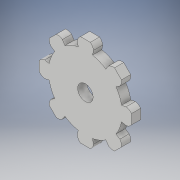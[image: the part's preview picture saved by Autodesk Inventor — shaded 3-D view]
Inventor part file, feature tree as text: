
AUTODESK INVENTOR PART (.ipt)
format: ipt  version: 2017 (Build 210142000, 142)  size: 165,376 bytes
history: native  units: in
note: dims shown in document units (in); Inventor stores cm internally (conversion verified against a paired STEP export)
features: extrude x2, sketch x2, pattern_circular x1
ambient origin geometry x8: Origin, YZ Plane, XZ Plane, XY Plane, X Axis, Y Axis, Z Axis, Center Point
bodies: Solid1 (feature_tree)
feature tree (5):
  extrude  "Extrusion1"  Depth=0.075in TaperAngle=0.0deg
  pattern_circular  "Circular Pattern1"  Count=8 Angle=360.0deg
  extrude  "Extrusion2"  Depth=0.075in TaperAngle=0.0deg
  sketch  "Sketch1"  dims[d0=0.6in d1=360.0deg d2=0.04in d3=0.04in d4=0.075in d5=0.075in d6=0.0in d7=3.1496in d8=360.0deg]
  sketch  "Sketch2"  dims[d10=0.126in d11=0.075in d12=0.0in]
